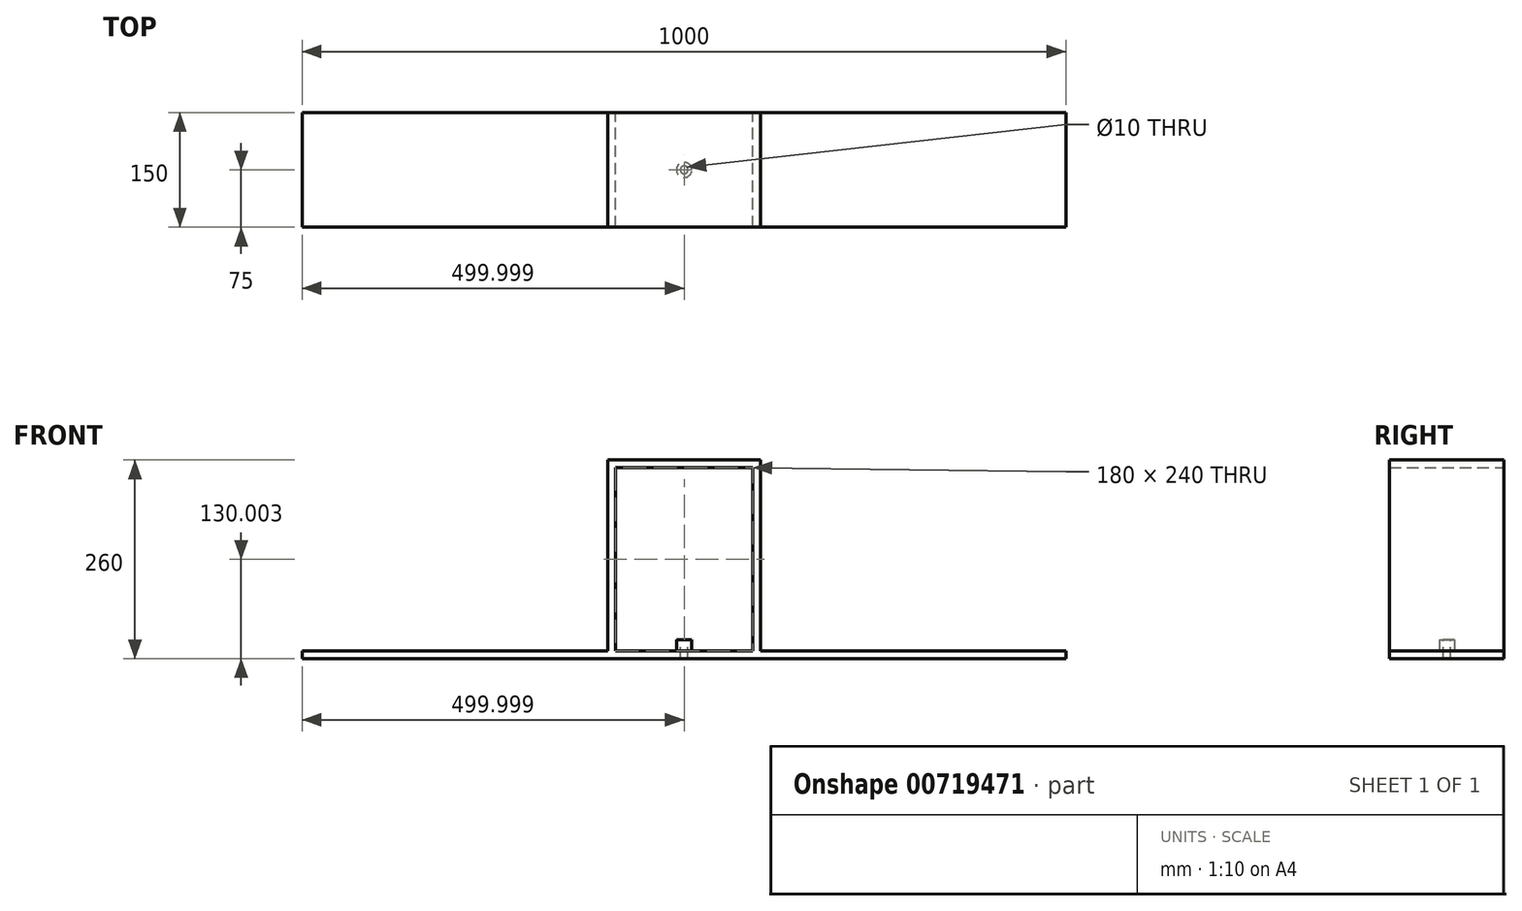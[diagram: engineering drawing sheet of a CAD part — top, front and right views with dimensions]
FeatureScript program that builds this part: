
annotation { "Feature Type Name" : "Feature", "Feature Type Description" : "" }
export const myFeature = defineFeature(function(context is Context, id is Id, definition is map)
    precondition{}
    {
        {
            var Q0;
            Q0=qCreatedBy(makeId("Front.planeOp"),FACE);
            var sketch = newSketch(context, id + "F0", { "sketchPlane" : qUnion([Q0])});
            skLineSegment(sketch, "E0.bottom", {"start": v(197.4, 274.36) * mm, "end": v(377.4, 274.36) * mm});
            skLineSegment(sketch, "E0.top", {"start": v(197.4, 34.36) * mm, "end": v(377.4, 34.36) * mm});
            skLineSegment(sketch, "E0.left", {"start": v(197.4, 274.36) * mm, "end": v(197.4, 34.36) * mm});
            skLineSegment(sketch, "E0.right", {"start": v(377.4, 274.36) * mm, "end": v(377.4, 34.36) * mm});
            skLineSegment(sketch, "E1", {"start": v(187.4, 284.36) * mm, "end": v(387.4, 284.36) * mm});
            skLineSegment(sketch, "E2", {"start": v(387.4, 284.36) * mm, "end": v(387.4, 34.36) * mm});
            skLineSegment(sketch, "E3", {"start": v(387.4, 34.36) * mm, "end": v(787.4, 34.36) * mm});
            skLineSegment(sketch, "E4", {"start": v(787.4, 34.36) * mm, "end": v(787.4, 24.36) * mm});
            skLineSegment(sketch, "E5", {"start": v(787.4, 24.36) * mm, "end": v(-212.6, 24.36) * mm});
            skLineSegment(sketch, "E6", {"start": v(-212.6, 24.36) * mm, "end": v(-212.6, 34.36) * mm});
            skLineSegment(sketch, "E7", {"start": v(-212.6, 34.36) * mm, "end": v(187.4, 34.36) * mm});
            skLineSegment(sketch, "E8", {"start": v(187.4, 34.36) * mm, "end": v(187.4, 284.36) * mm});
            skSolve(sketch);
        }
        {
            var Q0;
            Q0 = qSketchRegion(id + "F0", true);
            extrude(context, id + "F1", {"entities" : qUnion([Q0]), "endBound" : BoundingType.SYMMETRIC, "depth" : 150 * mm, "offsetDistance" : 25 * mm});
        }
        {
            var Q0;
            Q0=makeQuery(id+"F1.opExtrude","SWEPT_FACE",FACE,{"disambiguationData":[OSD([sQuery(id+"F0.wireOp",EDGE,"E0.top")])]});
            var sketch = newSketch(context, id + "F2", { "sketchPlane" : qUnion([Q0])});
            skLineSegment(sketch, "E9", {"start": v(287.4, 75) * mm, "end": v(287.4, -75) * mm, "construction": true});
            skLineSegment(sketch, "E10", {"start": v(0, 0) * mm, "end": v(287.4, 0) * mm, "construction": true});
            skCircle(sketch, "E11", {"center": v(287.4, 0) * mm, "radius": 5 * mm});
            skCircle(sketch, "E12", {"center": v(287.4, 0) * mm, "radius": 10 * mm});
            skSolve(sketch);
        }
        {
            var Q0;
            Q0=sQuery(id+"F2.wireOp",VERTEX,"E10.end");
            var Q1;
            Q1=makeQuery(id+"F1.opExtrude","SWEPT_BODY",BODY,{"disambiguationData":[OSD([sQuery(id+"F0.wireOp",EDGE,"E0.bottom"),sQuery(id+"F0.wireOp",EDGE,"E0.top"),sQuery(id+"F0.wireOp",EDGE,"E0.left"),sQuery(id+"F0.wireOp",EDGE,"E0.right"),sQuery(id+"F0.wireOp",EDGE,"E1"),sQuery(id+"F0.wireOp",EDGE,"E2"),sQuery(id+"F0.wireOp",EDGE,"E3"),sQuery(id+"F0.wireOp",EDGE,"E4"),sQuery(id+"F0.wireOp",EDGE,"E5"),sQuery(id+"F0.wireOp",EDGE,"E6"),sQuery(id+"F0.wireOp",EDGE,"E7"),sQuery(id+"F0.wireOp",EDGE,"E8")])]});
            hole(context, id + "F3", {"style" : HoleStyle.SIMPLE, "endStyle" : HoleEndStyle.BLIND, "holeDiameter" : 10 * mm, "majorDiameter" : 5 * mm, "holeDepth" : 600 * mm, "isTappedThrough" : true, "tappedDepth" : 12 * mm, "tapClearance" : 3, "startFromSketch" : true, "locations" : qUnion([Q0]), "scope" : qUnion([Q1])});
        }
        {
            var Q0;
            Q0=makeQuery(id+"F2.imprint","IMPRINT",FACE,{"disambiguationData":[TD([[makeQuery(id+"F2.imprint","IMPRINT",EDGE,{"derivedFrom":sQuery(id+"F2.wireOp",EDGE,"E11")}),-1.0]])]});
            extrude(context, id + "F4", {"entities" : qUnion([Q0]), "operationType" : NewBodyOperationType.ADD, "depth" : 15 * mm, "offsetDistance" : 25 * mm});
        }
    });
